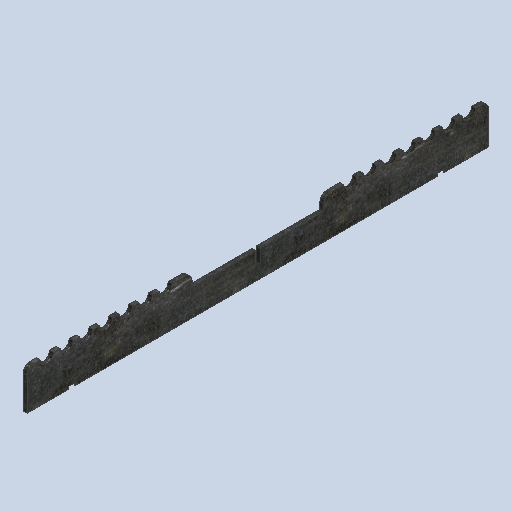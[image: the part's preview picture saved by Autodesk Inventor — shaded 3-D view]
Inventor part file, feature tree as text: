
AUTODESK INVENTOR PART (.ipt)
format: ipt  version: 2024.3 (Build 283343000, 343)  size: 340,480 bytes
history: native  units: mm
features: extrude x3, sketch x3, fillet x1, mirror x1, projected_geometry x1
ambient origin geometry x8: Origin, YZ Plane, XZ Plane, XY Plane, X Axis, Y Axis, Z Axis, Center Point
bodies: Solid1 (feature_tree)
feature tree (9):
  extrude  "Extrusion1"  Depth=350.0mm
  extrude  "Extrusion2"  Depth=100.0mm
  fillet  "Fillet1"  Radius=20.0mm
  mirror  "Mirror1"
  extrude  "Extrusion3"  Depth=3.1mm
  sketch  "Sketch1"  dims[d0=30.0mm d1=350.0mm]
  sketch  "Sketch2"  dims[d2=0.0mm d3=100.0mm d4=20.0mm]
  sketch  "Sketch3"  dims[d5=20.0mm d6=3.1mm d7=3.0mm d8=0.0mm d9=10.0mm d10=10.0mm d11=10.0mm d12=10.0mm d13=10.0mm d14=10.0mm d15=10.0mm d16=15.0mm d17=15.0mm d18=15.0mm d19=15.0mm d20=15.0mm d21=15.0mm d22=15.0mm d23=3.0mm d24=0.0mm d25=5.0mm d26=3.0mm d27=45.0deg d28=3.0mm d29=195.0mm d31=2.0mm d32=0.0mm d33=97.5mm]
  projected_geometry  "Projected Loop1"
